# Revit family: 3064600 + 3064606 Lighting Fixture_Sylvania_Steg 260 Wall_Surface Mounted
name_source: partatom
category: Lighting Fixtures
revit_build: Autodesk Revit 2017 (Build: 20190507_1515(x64)
units: mm (PartAtom-declared; Revit-internal decimal feet)

## family parameters
Cut with Voids When Loaded = No
Host = Face
Light Source = Yes
OmniClass Number = 23.80.70.11.17
OmniClass Title = Specialized Lighting by Location or Use
Part Type = Normal
Room Calculation Point = No
Round Connector Dimension = Use Diameter
Shared = No

## types (1)
- STEG 260 WALL TRIM RHS WHITE + DECOR HUB SMALL LED 2700K EB
    Apparent Load = 11 VA
    Assembly Code = D5020200
    Body Material = Polycarbonate_Steg_White
    CRI (Ra) = 85
    Catalog Number = 3064600 STEG 260 WALL TRIM RHS WHITE + 3064606 DECOR HUB SMALL LED 2700K EB
    Color Filter = 16777215
    Default Elevation = 0 mm  [stored 0 ft]
    Description = Steg is a range of ambient LED luminaires, consisting of wall mounted, pendant, table and floor lamp options A complete product family retaining a core design language Influenced by the faceted design trend, the wall version allows for unique and personalized installations to be created by architects, designers and end users Tailored with hospitality in mind; suitable for restaurants, cafes, lounge spaces, reception areas, bars and hotels Amber white (2,700K) colour temperature provides an ambient lighting effect that’s perfect for creating a relaxing environment 4,000K colour temperature also available 1 standard body colour: matte white Custom colours available upon request - please consult your local sales force for more information Through its faceted design, it offers complete freedom to the end user through the ability to create infinite lighting features on a surface Start by specifying the desired LED Decor Hub and the equivalent sized Wall trim Direct/indirect lighting Available in 2 sizes: - Small (260mm): lumen output equivalent to a 75W QT32 halogen or 2x13W CFL product - Large (400mm): lumen output equivalent to a 100W QT32 halogen or 2x18W CFL product
    Diffuser Material = Polycarbonate_Steg_Opal_2700K
    Dimming Lamp Color Temperature Shift = <None>
    Distribution Type = Direct/indirect
    Drive Current = 700mA
    Energy Class = A++, A+, A
    Hub Material = Metal_Sylvania_Steg_Silver
    IP Rating = IP20
    LHS = No
    LOR = 100 %
    Lamp = Integrated LED
    Lamp Comments = 2 x 5.5W
    Life = 50 000h
    Manufacturer = Feilo Sylvania
    Model = STEG 260 WALL TRIM RHS WHITE + DECOR HUB SMALL LED 2700K EB
    Photometric Web File = 3064600+3064606_Steg260WallTrimRHSWhite+DecorHubSmallLED2700KEB-192045.ies
    Product Family = STEG 260 WALL
    Product Page URL = http://www.sylvania-lighting.com
    RHS = Yes
    Tilt Angle = -90.00°
    URL = http://www.sylvania-lighting.com
    Voltage = 230 V
    Voltage Comments = UNV (Universal Voltage; 220-240 Volt)

note: [stored X ft] marks values corroborated as IEEE doubles in the binary element streams (Revit-internal decimal feet)

## geometry (parser evidence)
native form markers: Blend x6, Sweep x1
no freeform markers — native parametric forms only
